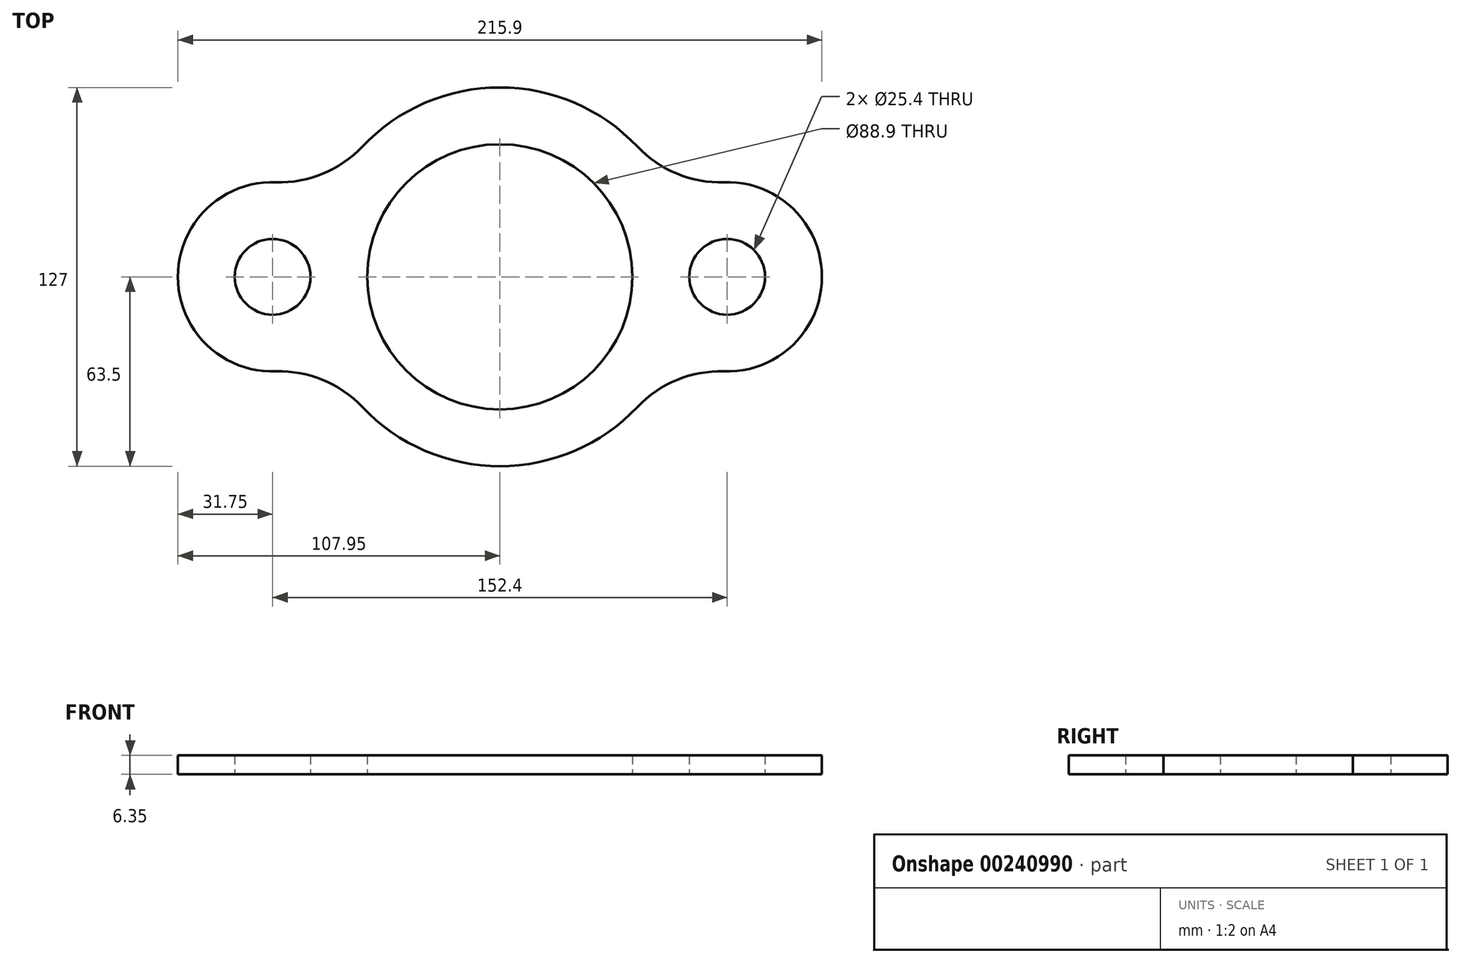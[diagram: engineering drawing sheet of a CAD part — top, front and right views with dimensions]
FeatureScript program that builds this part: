
annotation { "Feature Type Name" : "Feature", "Feature Type Description" : "" }
export const myFeature = defineFeature(function(context is Context, id is Id, definition is map)
    precondition{}
    {
        {
            var Q0;
            Q0=qCreatedBy(makeId("Top.planeOp"),FACE);
            var sketch = newSketch(context, id + "F0", { "sketchPlane" : qUnion([Q0])});
            skCircle(sketch, "E0", {"center": v(0, 0) * mm, "radius": 44.45 * mm});
            skCircle(sketch, "E1", {"center": v(76.2, 0) * mm, "radius": 12.7 * mm});
            skCircle(sketch, "E2", {"center": v(-76.2, 0) * mm, "radius": 12.7 * mm});
            skArc(sketch, "E3", {"start": v(75.12, -31.73) * mm, "mid": v(107.95, 0) * mm, "end": v(75.12, 31.73) * mm});
            skArc(sketch, "E4", {"start": v(-75.12, 31.73) * mm, "mid": v(-107.95, 0) * mm, "end": v(-75.12, -31.73) * mm});
            skArc(sketch, "E5", {"start": v(-46.14, -43.63) * mm, "mid": v(0, -63.5) * mm, "end": v(46.14, -43.63) * mm});
            skArc(sketch, "E6.trimOffspring", {"start": v(46.14, 43.63) * mm, "mid": v(0, 63.5) * mm, "end": v(-46.14, 43.63) * mm});
            skPoint(sketch, "E7.visualSharp", {"position": v(-57.94, 25.98) * mm});
            skArc(sketch, "E7.filletArc", {"start": v(-75.12, 31.73) * mm, "mid": v(-59.35, 34.56) * mm, "end": v(-46.14, 43.63) * mm});
            skPoint(sketch, "E8.visualSharp", {"position": v(-57.94, -25.98) * mm});
            skArc(sketch, "E8.filletArc", {"start": v(-46.14, -43.63) * mm, "mid": v(-59.35, -34.56) * mm, "end": v(-75.12, -31.73) * mm});
            skPoint(sketch, "E9.visualSharp", {"position": v(57.94, -25.98) * mm});
            skArc(sketch, "E9.filletArc", {"start": v(75.12, -31.73) * mm, "mid": v(59.35, -34.56) * mm, "end": v(46.14, -43.63) * mm});
            skPoint(sketch, "E10.visualSharp", {"position": v(57.94, 25.98) * mm});
            skArc(sketch, "E10.filletArc", {"start": v(46.14, 43.63) * mm, "mid": v(59.35, 34.56) * mm, "end": v(75.12, 31.73) * mm});
            skSolve(sketch);
        }
        {
            var Q0;
            Q0 = qSketchRegion(id + "F0", true);
            extrude(context, id + "F1", {"entities" : qUnion([Q0]), "depth" : 6.35 * mm});
        }
    });
